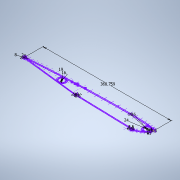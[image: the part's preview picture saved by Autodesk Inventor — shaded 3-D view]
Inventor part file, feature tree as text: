
AUTODESK INVENTOR PART (.ipt)
format: ipt  version: 2022 (Build 260153000, 153)  size: 223,232 bytes
history: native  units: mm
features: sketch x1
ambient origin geometry x8: Origin, YZ Plane, XZ Plane, XY Plane, X Axis, Y Axis, Z Axis, Center Point
feature tree (1):
  sketch  "Sketch1"  dims[d31=34.456mm d50=368.759386mm d57=16.0mm d69=8.0mm d80=19.0mm d81=16.0mm d82=1.0mm d83=1.0mm d84=1.0mm d85=1.0mm d86=1.0mm d87=0.8mm d88=1.0mm d90=19.0mm d94=5.0mm d95=5.0mm d105=5.0mm d106=5.0mm d108=2.0mm d114=5.0mm d115=5.0mm d116=24.0mm d117=2.5mm d118=2.5mm d123=2.5mm d124=2.5mm d125=10.0mm d126=24.0mm d127=24.0mm d128=27.0mm d131=0.5mm d132=0.872665mm d133=0.5mm d134=0.872665mm]
